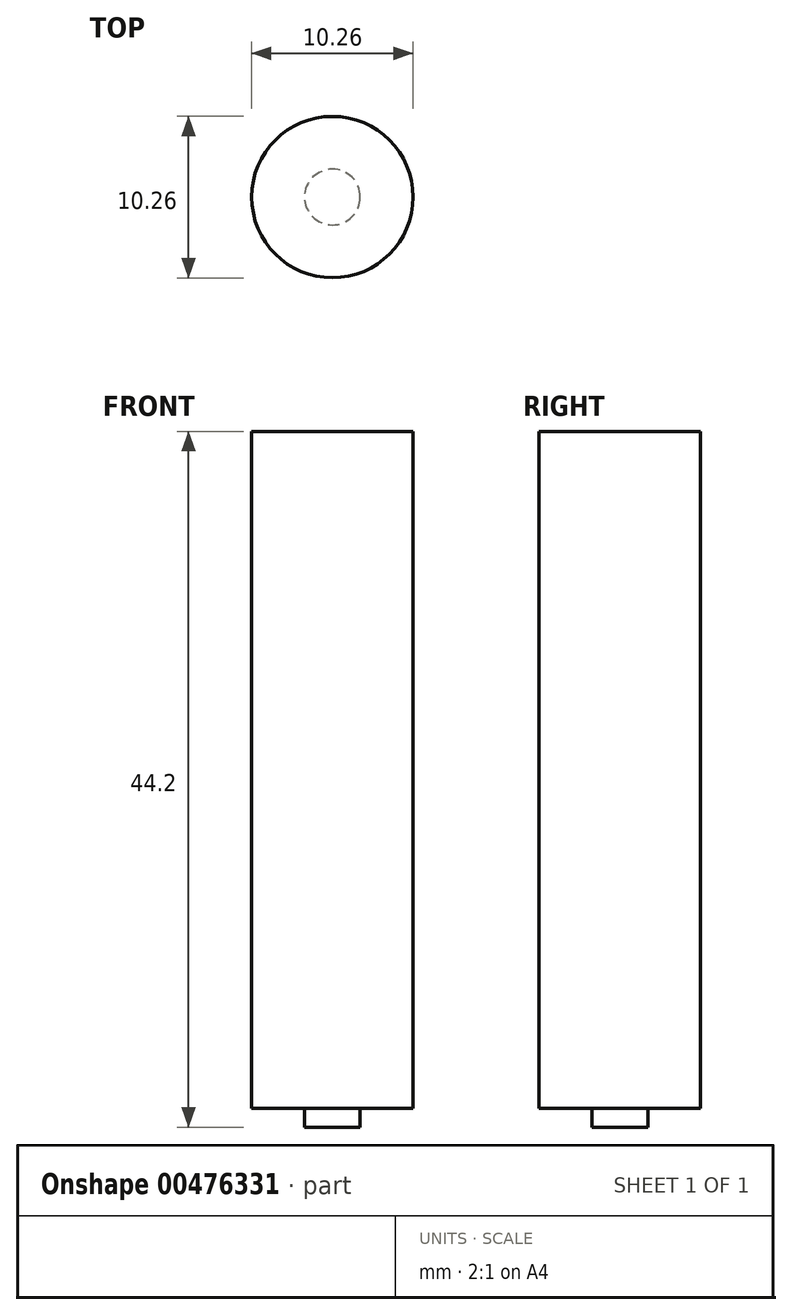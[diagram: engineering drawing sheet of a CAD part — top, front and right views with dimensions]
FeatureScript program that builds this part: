
annotation { "Feature Type Name" : "Feature", "Feature Type Description" : "" }
export const myFeature = defineFeature(function(context is Context, id is Id, definition is map)
    precondition{}
    {
        {
            var Q0;
            Q0=qCreatedBy(makeId("Top.planeOp"),FACE);
            var sketch = newSketch(context, id + "F0", { "sketchPlane" : qUnion([Q0])});
            skCircle(sketch, "E0", {"center": v(0, 0) * mm, "radius": 5.12 * mm});
            skCircle(sketch, "E1", {"center": v(0, 0) * mm, "radius": 1.77 * mm});
            skSolve(sketch);
        }
        {
            var Q0;
            Q0=qSketchRegion(id+"F0",true);
            var Q1;
            Q1=makeQuery(id+"F0.imprint","IMPRINT",FACE,{"disambiguationData":[TD([[makeQuery(id+"F0.imprint","IMPRINT",EDGE,{"derivedFrom":sQuery(id+"F0.wireOp",EDGE,"E1")}),1.0]])]});
            extrude(context, id + "F1", {"entities" : qUnion([Q0, Q1]), "depth" : 43 * mm});
        }
        {
            var Q0;
            Q0=makeQuery(id+"F0.imprint","IMPRINT",FACE,{"disambiguationData":[TD([[makeQuery(id+"F0.imprint","IMPRINT",EDGE,{"derivedFrom":sQuery(id+"F0.wireOp",EDGE,"E1")}),1.0]])]});
            extrude(context, id + "F2", {"entities" : qUnion([Q0]), "operationType" : NewBodyOperationType.ADD, "oppositeDirection" : true, "depth" : 1.2 * mm});
        }
    });
